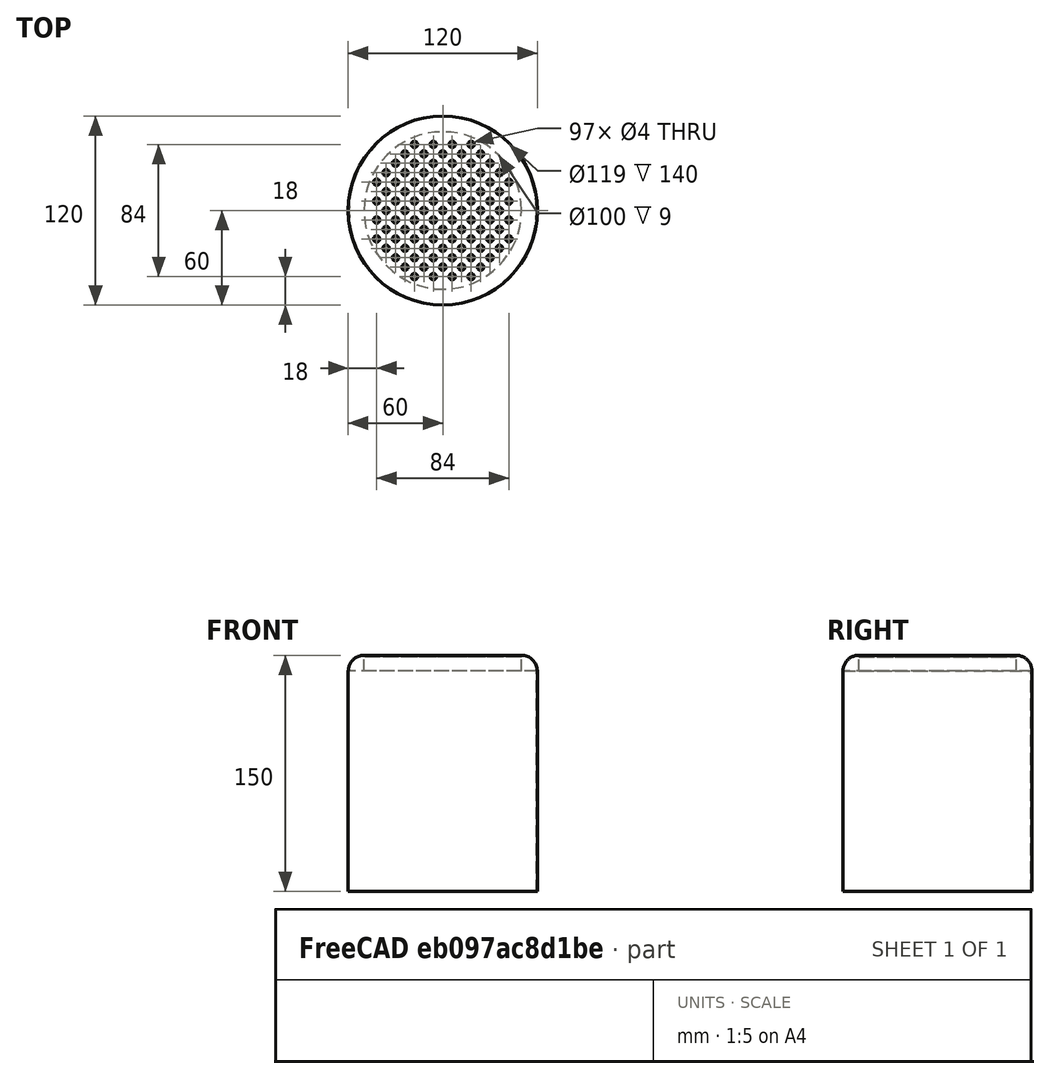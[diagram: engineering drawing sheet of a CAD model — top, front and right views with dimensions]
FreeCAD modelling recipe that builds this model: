
FCSTD DOCUMENT  (FreeCAD 0.18R4 (GitTag))
Label: 3
License: All rights reserved
LicenseURL: http://en.wikipedia.org/wiki/All_rights_reserved
objects: Part::Cylinder×100, Part::Cut×3, Part::Fillet×1, Part::Compound×1
note: 105 computed .brp shape members not serialized (recipe doc carries the construction recipe); baked Part::Feature solids carry a one-line shape summary decoded from their .brp

FEATURE [Part::Cylinder] Cylinder  label="Cilindro"
  Angle = 360
  AttacherType = Attacher::AttachEngine3D
  Height = 150
  Radius = 60
FEATURE [Part::Fillet] Fillet
  Base = -> Cylinder
  Edges = 1 edges r=10: [Edge1]
FEATURE [Part::Cylinder] Cylinder001  label="Cilindro001"
  Angle = 360
  AttacherType = Attacher::AttachEngine3D
  Height = 140
  Radius = 59.5
FEATURE [Part::Cut] Cut
  Base = -> Fillet
  Tool = -> Cylinder001
FEATURE [Part::Cylinder] Cylinder002  label="Cilindro002"
  Angle = 360
  AttacherType = Attacher::AttachEngine3D
  Height = 10
  Placement = pos=(0,0,139) rot=(0,0,1;0rad)
  Radius = 50
FEATURE [Part::Cut] Cut001
  Base = -> Cut
  Tool = -> Cylinder002
FEATURE [Part::Cylinder] Cylinder005  label="Cilindro005"
  Angle = 360
  AttacherType = Attacher::AttachEngine3D
  Height = 200
  Radius = 2
FEATURE [Part::Cylinder] Cylinder006  label="Cilindro006"
  Angle = 360
  AttacherType = Attacher::AttachEngine3D
  Height = 200
  Placement = pos=(6,-6,0) rot=(0,0,1;0rad)
  Radius = 2
FEATURE [Part::Cylinder] Cylinder007  label="Cilindro007"
  Angle = 360
  AttacherType = Attacher::AttachEngine3D
  Height = 200
  Placement = pos=(6,6,0) rot=(0,0,1;0rad)
  Radius = 2
FEATURE [Part::Cylinder] Cylinder008  label="Cilindro008"
  Angle = 360
  AttacherType = Attacher::AttachEngine3D
  Height = 200
  Placement = pos=(6,18,0) rot=(0,0,1;0rad)
  Radius = 2
FEATURE [Part::Cylinder] Cylinder009  label="Cilindro009"
  Angle = 360
  AttacherType = Attacher::AttachEngine3D
  Height = 200
  Placement = pos=(0,12,0) rot=(0,0,1;0rad)
  Radius = 2
FEATURE [Part::Cylinder] Cylinder010  label="Cilindro010"
  Angle = 360
  AttacherType = Attacher::AttachEngine3D
  Height = 200
  Placement = pos=(0,24,0) rot=(0,0,1;0rad)
  Radius = 2
FEATURE [Part::Cylinder] Cylinder011  label="Cilindro011"
  Angle = 360
  AttacherType = Attacher::AttachEngine3D
  Height = 200
  Placement = pos=(6,30,0) rot=(0,0,1;0rad)
  Radius = 2
FEATURE [Part::Cylinder] Cylinder012  label="Cilindro012"
  Angle = 360
  AttacherType = Attacher::AttachEngine3D
  Height = 200
  Placement = pos=(0,36,0) rot=(0,0,1;0rad)
  Radius = 2
FEATURE [Part::Cylinder] Cylinder013  label="Cilindro013"
  Angle = 360
  AttacherType = Attacher::AttachEngine3D
  Height = 200
  Placement = pos=(6,42,0) rot=(0,0,1;0rad)
  Radius = 2
FEATURE [Part::Cylinder] Cylinder014  label="Cilindro014"
  Angle = 360
  AttacherType = Attacher::AttachEngine3D
  Height = 200
  Placement = pos=(6,-42,0) rot=(0,0,1;0rad)
  Radius = 2
FEATURE [Part::Cylinder] Cylinder015  label="Cilindro015"
  Angle = 360
  AttacherType = Attacher::AttachEngine3D
  Height = 200
  Placement = pos=(6,-30,0) rot=(0,0,1;0rad)
  Radius = 2
FEATURE [Part::Cylinder] Cylinder016  label="Cilindro016"
  Angle = 360
  AttacherType = Attacher::AttachEngine3D
  Height = 200
  Placement = pos=(6,-18,0) rot=(0,0,1;0rad)
  Radius = 2
FEATURE [Part::Cylinder] Cylinder017  label="Cilindro017"
  Angle = 360
  AttacherType = Attacher::AttachEngine3D
  Height = 200
  Placement = pos=(0,-36,0) rot=(0,0,1;0rad)
  Radius = 2
FEATURE [Part::Cylinder] Cylinder018  label="Cilindro018"
  Angle = 360
  AttacherType = Attacher::AttachEngine3D
  Height = 200
  Placement = pos=(0,-24,0) rot=(0,0,1;0rad)
  Radius = 2
FEATURE [Part::Cylinder] Cylinder019  label="Cilindro019"
  Angle = 360
  AttacherType = Attacher::AttachEngine3D
  Height = 200
  Placement = pos=(0,-12,0) rot=(0,0,1;0rad)
  Radius = 2
FEATURE [Part::Cylinder] Cylinder020  label="Cilindro020"
  Angle = 360
  AttacherType = Attacher::AttachEngine3D
  Height = 200
  Placement = pos=(-6,6,0) rot=(0,0,1;0rad)
  Radius = 2
FEATURE [Part::Cylinder] Cylinder021  label="Cilindro021"
  Angle = 360
  AttacherType = Attacher::AttachEngine3D
  Height = 200
  Placement = pos=(-6,18,0) rot=(0,0,1;0rad)
  Radius = 2
FEATURE [Part::Cylinder] Cylinder022  label="Cilindro022"
  Angle = 360
  AttacherType = Attacher::AttachEngine3D
  Height = 200
  Placement = pos=(-6,30,0) rot=(0,0,1;0rad)
  Radius = 2
FEATURE [Part::Cylinder] Cylinder023  label="Cilindro023"
  Angle = 360
  AttacherType = Attacher::AttachEngine3D
  Height = 200
  Placement = pos=(-6,42,0) rot=(0,0,1;0rad)
  Radius = 2
FEATURE [Part::Cylinder] Cylinder024  label="Cilindro024"
  Angle = 360
  AttacherType = Attacher::AttachEngine3D
  Height = 200
  Placement = pos=(-6,-6,0) rot=(0,0,1;0rad)
  Radius = 2
FEATURE [Part::Cylinder] Cylinder025  label="Cilindro025"
  Angle = 360
  AttacherType = Attacher::AttachEngine3D
  Height = 200
  Placement = pos=(-6,-18,0) rot=(0,0,1;0rad)
  Radius = 2
FEATURE [Part::Cylinder] Cylinder026  label="Cilindro026"
  Angle = 360
  AttacherType = Attacher::AttachEngine3D
  Height = 200
  Placement = pos=(-6,-30,0) rot=(0,0,1;0rad)
  Radius = 2
FEATURE [Part::Cylinder] Cylinder027  label="Cilindro027"
  Angle = 360
  AttacherType = Attacher::AttachEngine3D
  Height = 200
  Placement = pos=(-6,-42,0) rot=(0,0,1;0rad)
  Radius = 2
FEATURE [Part::Cylinder] Cylinder028  label="Cilindro028"
  Angle = 360
  AttacherType = Attacher::AttachEngine3D
  Height = 200
  Placement = pos=(12,0,0) rot=(0,0,1;0rad)
  Radius = 2
FEATURE [Part::Cylinder] Cylinder029  label="Cilindro029"
  Angle = 360
  AttacherType = Attacher::AttachEngine3D
  Height = 200
  Placement = pos=(12,12,0) rot=(0,0,1;0rad)
  Radius = 2
FEATURE [Part::Cylinder] Cylinder030  label="Cilindro030"
  Angle = 360
  AttacherType = Attacher::AttachEngine3D
  Height = 200
  Placement = pos=(12,24,0) rot=(0,0,1;0rad)
  Radius = 2
FEATURE [Part::Cylinder] Cylinder031  label="Cilindro031"
  Angle = 360
  AttacherType = Attacher::AttachEngine3D
  Height = 200
  Placement = pos=(12,36,0) rot=(0,0,1;0rad)
  Radius = 2
FEATURE [Part::Cylinder] Cylinder032  label="Cilindro032"
  Angle = 360
  AttacherType = Attacher::AttachEngine3D
  Height = 200
  Placement = pos=(12,-24,0) rot=(0,0,1;0rad)
  Radius = 2
FEATURE [Part::Cylinder] Cylinder033  label="Cilindro033"
  Angle = 360
  AttacherType = Attacher::AttachEngine3D
  Height = 200
  Placement = pos=(12,-36,0) rot=(0,0,1;0rad)
  Radius = 2
FEATURE [Part::Cylinder] Cylinder034  label="Cilindro034"
  Angle = 360
  AttacherType = Attacher::AttachEngine3D
  Height = 200
  Placement = pos=(12,-12,0) rot=(0,0,1;0rad)
  Radius = 2
FEATURE [Part::Cylinder] Cylinder035  label="Cilindro035"
  Angle = 360
  AttacherType = Attacher::AttachEngine3D
  Height = 200
  Placement = pos=(-12,0,0) rot=(0,0,1;0rad)
  Radius = 2
FEATURE [Part::Cylinder] Cylinder036  label="Cilindro036"
  Angle = 360
  AttacherType = Attacher::AttachEngine3D
  Height = 200
  Placement = pos=(-12,12,0) rot=(0,0,1;0rad)
  Radius = 2
FEATURE [Part::Cylinder] Cylinder037  label="Cilindro037"
  Angle = 360
  AttacherType = Attacher::AttachEngine3D
  Height = 200
  Placement = pos=(-12,24,0) rot=(0,0,1;0rad)
  Radius = 2
FEATURE [Part::Cylinder] Cylinder038  label="Cilindro038"
  Angle = 360
  AttacherType = Attacher::AttachEngine3D
  Height = 200
  Placement = pos=(-12,36,0) rot=(0,0,1;0rad)
  Radius = 2
FEATURE [Part::Cylinder] Cylinder039  label="Cilindro039"
  Angle = 360
  AttacherType = Attacher::AttachEngine3D
  Height = 200
  Placement = pos=(-12,-24,0) rot=(0,0,1;0rad)
  Radius = 2
FEATURE [Part::Cylinder] Cylinder040  label="Cilindro040"
  Angle = 360
  AttacherType = Attacher::AttachEngine3D
  Height = 200
  Placement = pos=(-12,-36,0) rot=(0,0,1;0rad)
  Radius = 2
FEATURE [Part::Cylinder] Cylinder041  label="Cilindro041"
  Angle = 360
  AttacherType = Attacher::AttachEngine3D
  Height = 200
  Placement = pos=(-12,-12,0) rot=(0,0,1;0rad)
  Radius = 2
FEATURE [Part::Cylinder] Cylinder042  label="Cilindro042"
  Angle = 360
  AttacherType = Attacher::AttachEngine3D
  Height = 200
  Placement = pos=(-24,-12,0) rot=(0,0,1;0rad)
  Radius = 2
FEATURE [Part::Cylinder] Cylinder043  label="Cilindro043"
  Angle = 360
  AttacherType = Attacher::AttachEngine3D
  Height = 200
  Placement = pos=(-24,-36,0) rot=(0,0,1;0rad)
  Radius = 2
FEATURE [Part::Cylinder] Cylinder044  label="Cilindro044"
  Angle = 360
  AttacherType = Attacher::AttachEngine3D
  Height = 200
  Placement = pos=(-24,-24,0) rot=(0,0,1;0rad)
  Radius = 2
FEATURE [Part::Cylinder] Cylinder045  label="Cilindro045"
  Angle = 360
  AttacherType = Attacher::AttachEngine3D
  Height = 200
  Placement = pos=(-24,36,0) rot=(0,0,1;0rad)
  Radius = 2
FEATURE [Part::Cylinder] Cylinder046  label="Cilindro046"
  Angle = 360
  AttacherType = Attacher::AttachEngine3D
  Height = 200
  Placement = pos=(-24,24,0) rot=(0,0,1;0rad)
  Radius = 2
FEATURE [Part::Cylinder] Cylinder047  label="Cilindro047"
  Angle = 360
  AttacherType = Attacher::AttachEngine3D
  Height = 200
  Placement = pos=(-24,12,0) rot=(0,0,1;0rad)
  Radius = 2
FEATURE [Part::Cylinder] Cylinder048  label="Cilindro048"
  Angle = 360
  AttacherType = Attacher::AttachEngine3D
  Height = 200
  Placement = pos=(-24,0,0) rot=(0,0,1;0rad)
  Radius = 2
FEATURE [Part::Cylinder] Cylinder049  label="Cilindro049"
  Angle = 360
  AttacherType = Attacher::AttachEngine3D
  Height = 200
  Placement = pos=(-18,6,0) rot=(0,0,1;0rad)
  Radius = 2
FEATURE [Part::Cylinder] Cylinder050  label="Cilindro050"
  Angle = 360
  AttacherType = Attacher::AttachEngine3D
  Height = 200
  Placement = pos=(-18,-42,0) rot=(0,0,1;0rad)
  Radius = 2
FEATURE [Part::Cylinder] Cylinder051  label="Cilindro051"
  Angle = 360
  AttacherType = Attacher::AttachEngine3D
  Height = 200
  Placement = pos=(-18,42,0) rot=(0,0,1;0rad)
  Radius = 2
FEATURE [Part::Cylinder] Cylinder052  label="Cilindro052"
  Angle = 360
  AttacherType = Attacher::AttachEngine3D
  Height = 200
  Placement = pos=(-18,18,0) rot=(0,0,1;0rad)
  Radius = 2
FEATURE [Part::Cylinder] Cylinder053  label="Cilindro053"
  Angle = 360
  AttacherType = Attacher::AttachEngine3D
  Height = 200
  Placement = pos=(-18,30,0) rot=(0,0,1;0rad)
  Radius = 2
FEATURE [Part::Cylinder] Cylinder054  label="Cilindro054"
  Angle = 360
  AttacherType = Attacher::AttachEngine3D
  Height = 200
  Placement = pos=(-18,-30,0) rot=(0,0,1;0rad)
  Radius = 2
FEATURE [Part::Cylinder] Cylinder055  label="Cilindro055"
  Angle = 360
  AttacherType = Attacher::AttachEngine3D
  Height = 200
  Placement = pos=(-18,-6,0) rot=(0,0,1;0rad)
  Radius = 2
FEATURE [Part::Cylinder] Cylinder056  label="Cilindro056"
  Angle = 360
  AttacherType = Attacher::AttachEngine3D
  Height = 200
  Placement = pos=(-18,-18,0) rot=(0,0,1;0rad)
  Radius = 2
FEATURE [Part::Cylinder] Cylinder057  label="Cilindro057"
  Angle = 360
  AttacherType = Attacher::AttachEngine3D
  Height = 200
  Placement = pos=(-30,-18,0) rot=(0,0,1;0rad)
  Radius = 2
FEATURE [Part::Cylinder] Cylinder059  label="Cilindro059"
  Angle = 360
  AttacherType = Attacher::AttachEngine3D
  Height = 200
  Placement = pos=(-30,18,0) rot=(0,0,1;0rad)
  Radius = 2
FEATURE [Part::Cylinder] Cylinder060  label="Cilindro060"
  Angle = 360
  AttacherType = Attacher::AttachEngine3D
  Height = 200
  Placement = pos=(-30,30,0) rot=(0,0,1;0rad)
  Radius = 2
FEATURE [Part::Cylinder] Cylinder061  label="Cilindro061"
  Angle = 360
  AttacherType = Attacher::AttachEngine3D
  Height = 200
  Placement = pos=(-30,-30,0) rot=(0,0,1;0rad)
  Radius = 2
FEATURE [Part::Cylinder] Cylinder062  label="Cilindro062"
  Angle = 360
  AttacherType = Attacher::AttachEngine3D
  Height = 200
  Placement = pos=(-30,-6,0) rot=(0,0,1;0rad)
  Radius = 2
FEATURE [Part::Cylinder] Cylinder064  label="Cilindro064"
  Angle = 360
  AttacherType = Attacher::AttachEngine3D
  Height = 200
  Placement = pos=(-30,6,0) rot=(0,0,1;0rad)
  Radius = 2
FEATURE [Part::Cylinder] Cylinder065  label="Cilindro065"
  Angle = 360
  AttacherType = Attacher::AttachEngine3D
  Height = 200
  Placement = pos=(-42,6,0) rot=(0,0,1;0rad)
  Radius = 2
FEATURE [Part::Cylinder] Cylinder066  label="Cilindro066"
  Angle = 360
  AttacherType = Attacher::AttachEngine3D
  Height = 200
  Placement = pos=(-42,-18,0) rot=(0,0,1;0rad)
  Radius = 2
FEATURE [Part::Cylinder] Cylinder068  label="Cilindro068"
  Angle = 360
  AttacherType = Attacher::AttachEngine3D
  Height = 200
  Placement = pos=(-42,-6,0) rot=(0,0,1;0rad)
  Radius = 2
FEATURE [Part::Cylinder] Cylinder069  label="Cilindro069"
  Angle = 360
  AttacherType = Attacher::AttachEngine3D
  Height = 200
  Placement = pos=(-42,18,0) rot=(0,0,1;0rad)
  Radius = 2
FEATURE [Part::Cylinder] Cylinder070  label="Cilindro070"
  Angle = 360
  AttacherType = Attacher::AttachEngine3D
  Height = 200
  Placement = pos=(24,0,0) rot=(0,0,1;0rad)
  Radius = 2
FEATURE [Part::Cylinder] Cylinder071  label="Cilindro071"
  Angle = 360
  AttacherType = Attacher::AttachEngine3D
  Height = 200
  Placement = pos=(24,24,0) rot=(0,0,1;0rad)
  Radius = 2
FEATURE [Part::Cylinder] Cylinder072  label="Cilindro072"
  Angle = 360
  AttacherType = Attacher::AttachEngine3D
  Height = 200
  Placement = pos=(24,36,0) rot=(0,0,1;0rad)
  Radius = 2
FEATURE [Part::Cylinder] Cylinder073  label="Cilindro073"
  Angle = 360
  AttacherType = Attacher::AttachEngine3D
  Height = 200
  Placement = pos=(24,12,0) rot=(0,0,1;0rad)
  Radius = 2
FEATURE [Part::Cylinder] Cylinder074  label="Cilindro074"
  Angle = 360
  AttacherType = Attacher::AttachEngine3D
  Height = 200
  Placement = pos=(24,-36,0) rot=(0,0,1;0rad)
  Radius = 2
FEATURE [Part::Cylinder] Cylinder075  label="Cilindro075"
  Angle = 360
  AttacherType = Attacher::AttachEngine3D
  Height = 200
  Placement = pos=(24,-24,0) rot=(0,0,1;0rad)
  Radius = 2
FEATURE [Part::Cylinder] Cylinder076  label="Cilindro076"
  Angle = 360
  AttacherType = Attacher::AttachEngine3D
  Height = 200
  Placement = pos=(24,-12,0) rot=(0,0,1;0rad)
  Radius = 2
FEATURE [Part::Cylinder] Cylinder077  label="Cilindro077"
  Angle = 360
  AttacherType = Attacher::AttachEngine3D
  Height = 200
  Placement = pos=(36,-12,0) rot=(0,0,1;0rad)
  Radius = 2
FEATURE [Part::Cylinder] Cylinder079  label="Cilindro079"
  Angle = 360
  AttacherType = Attacher::AttachEngine3D
  Height = 200
  Placement = pos=(36,12,0) rot=(0,0,1;0rad)
  Radius = 2
FEATURE [Part::Cylinder] Cylinder081  label="Cilindro081"
  Angle = 360
  AttacherType = Attacher::AttachEngine3D
  Height = 200
  Placement = pos=(36,0,0) rot=(0,0,1;0rad)
  Radius = 2
FEATURE [Part::Cylinder] Cylinder082  label="Cilindro082"
  Angle = 360
  AttacherType = Attacher::AttachEngine3D
  Height = 200
  Placement = pos=(36,24,0) rot=(0,0,1;0rad)
  Radius = 2
FEATURE [Part::Cylinder] Cylinder083  label="Cilindro083"
  Angle = 360
  AttacherType = Attacher::AttachEngine3D
  Height = 200
  Placement = pos=(36,-24,0) rot=(0,0,1;0rad)
  Radius = 2
FEATURE [Part::Cylinder] Cylinder084  label="Cilindro084"
  Angle = 360
  AttacherType = Attacher::AttachEngine3D
  Height = 200
  Placement = pos=(18,-6,0) rot=(0,0,1;0rad)
  Radius = 2
FEATURE [Part::Cylinder] Cylinder085  label="Cilindro085"
  Angle = 360
  AttacherType = Attacher::AttachEngine3D
  Height = 200
  Placement = pos=(18,6,0) rot=(0,0,1;0rad)
  Radius = 2
FEATURE [Part::Cylinder] Cylinder086  label="Cilindro086"
  Angle = 360
  AttacherType = Attacher::AttachEngine3D
  Height = 200
  Placement = pos=(18,18,0) rot=(0,0,1;0rad)
  Radius = 2
FEATURE [Part::Cylinder] Cylinder087  label="Cilindro087"
  Angle = 360
  AttacherType = Attacher::AttachEngine3D
  Height = 200
  Placement = pos=(18,30,0) rot=(0,0,1;0rad)
  Radius = 2
FEATURE [Part::Cylinder] Cylinder088  label="Cilindro088"
  Angle = 360
  AttacherType = Attacher::AttachEngine3D
  Height = 200
  Placement = pos=(18,42,0) rot=(0,0,1;0rad)
  Radius = 2
FEATURE [Part::Cylinder] Cylinder089  label="Cilindro089"
  Angle = 360
  AttacherType = Attacher::AttachEngine3D
  Height = 200
  Placement = pos=(18,-42,0) rot=(0,0,1;0rad)
  Radius = 2
FEATURE [Part::Cylinder] Cylinder090  label="Cilindro090"
  Angle = 360
  AttacherType = Attacher::AttachEngine3D
  Height = 200
  Placement = pos=(18,-30,0) rot=(0,0,1;0rad)
  Radius = 2
FEATURE [Part::Cylinder] Cylinder091  label="Cilindro091"
  Angle = 360
  AttacherType = Attacher::AttachEngine3D
  Height = 200
  Placement = pos=(18,-18,0) rot=(0,0,1;0rad)
  Radius = 2
FEATURE [Part::Cylinder] Cylinder092  label="Cilindro092"
  Angle = 360
  AttacherType = Attacher::AttachEngine3D
  Height = 200
  Placement = pos=(30,-18,0) rot=(0,0,1;0rad)
  Radius = 2
FEATURE [Part::Cylinder] Cylinder094  label="Cilindro094"
  Angle = 360
  AttacherType = Attacher::AttachEngine3D
  Height = 200
  Placement = pos=(30,18,0) rot=(0,0,1;0rad)
  Radius = 2
FEATURE [Part::Cylinder] Cylinder095  label="Cilindro095"
  Angle = 360
  AttacherType = Attacher::AttachEngine3D
  Height = 200
  Placement = pos=(30,30,0) rot=(0,0,1;0rad)
  Radius = 2
FEATURE [Part::Cylinder] Cylinder097  label="Cilindro097"
  Angle = 360
  AttacherType = Attacher::AttachEngine3D
  Height = 200
  Placement = pos=(30,-30,0) rot=(0,0,1;0rad)
  Radius = 2
FEATURE [Part::Cylinder] Cylinder098  label="Cilindro098"
  Angle = 360
  AttacherType = Attacher::AttachEngine3D
  Height = 200
  Placement = pos=(30,6,0) rot=(0,0,1;0rad)
  Radius = 2
FEATURE [Part::Cylinder] Cylinder099  label="Cilindro099"
  Angle = 360
  AttacherType = Attacher::AttachEngine3D
  Height = 200
  Placement = pos=(30,-6,0) rot=(0,0,1;0rad)
  Radius = 2
FEATURE [Part::Cylinder] Cylinder100  label="Cilindro100"
  Angle = 360
  AttacherType = Attacher::AttachEngine3D
  Height = 200
  Placement = pos=(42,-6,0) rot=(0,0,1;0rad)
  Radius = 2
FEATURE [Part::Cylinder] Cylinder101  label="Cilindro101"
  Angle = 360
  AttacherType = Attacher::AttachEngine3D
  Height = 200
  Placement = pos=(42,6,0) rot=(0,0,1;0rad)
  Radius = 2
FEATURE [Part::Cylinder] Cylinder102  label="Cilindro102"
  Angle = 360
  AttacherType = Attacher::AttachEngine3D
  Height = 200
  Placement = pos=(42,18,0) rot=(0,0,1;0rad)
  Radius = 2
FEATURE [Part::Cylinder] Cylinder105  label="Cilindro105"
  Angle = 360
  AttacherType = Attacher::AttachEngine3D
  Height = 200
  Placement = pos=(42,-18,0) rot=(0,0,1;0rad)
  Radius = 2
FEATURE [Part::Cylinder] Cylinder106  label="Cilindro106"
  Angle = 360
  AttacherType = Attacher::AttachEngine3D
  Height = 200
  Placement = pos=(-36,-12,0) rot=(0,0,1;0rad)
  Radius = 2
FEATURE [Part::Cylinder] Cylinder108  label="Cilindro108"
  Angle = 360
  AttacherType = Attacher::AttachEngine3D
  Height = 200
  Placement = pos=(-36,24,0) rot=(0,0,1;0rad)
  Radius = 2
FEATURE [Part::Cylinder] Cylinder109  label="Cilindro109"
  Angle = 360
  AttacherType = Attacher::AttachEngine3D
  Height = 200
  Placement = pos=(-36,12,0) rot=(0,0,1;0rad)
  Radius = 2
FEATURE [Part::Cylinder] Cylinder110  label="Cilindro110"
  Angle = 360
  AttacherType = Attacher::AttachEngine3D
  Height = 200
  Placement = pos=(-36,-24,0) rot=(0,0,1;0rad)
  Radius = 2
FEATURE [Part::Cylinder] Cylinder111  label="Cilindro111"
  Angle = 360
  AttacherType = Attacher::AttachEngine3D
  Height = 200
  Placement = pos=(-36,0,0) rot=(0,0,1;0rad)
  Radius = 2
FEATURE [Part::Compound] Compound
  Links = -> [Cylinder006,Cylinder027,Cylinder019,Cylinder030,Cylinder023,Cylinder021,Cylinder022,Cylinder026,Cylinder031,Cylinder017,Cylinder020,Cylinder024,Cylinder018,Cylinder025,Cylinder015,Cylinder016,Cylinder028,Cylinder013,Cylinder029,Cylinder007,Cylinder009,Cylinder083,Cylinder010,Cylinder008,Cylinder014,Cylinder011,Cylinder012,Cylinder045,Cylinder046,Cylinder047,Cylinder036,Cylinder040,Cylinder035,+64 more]
FEATURE [Part::Cut] Cut002
  Base = -> Cut001
  Tool = -> Compound
